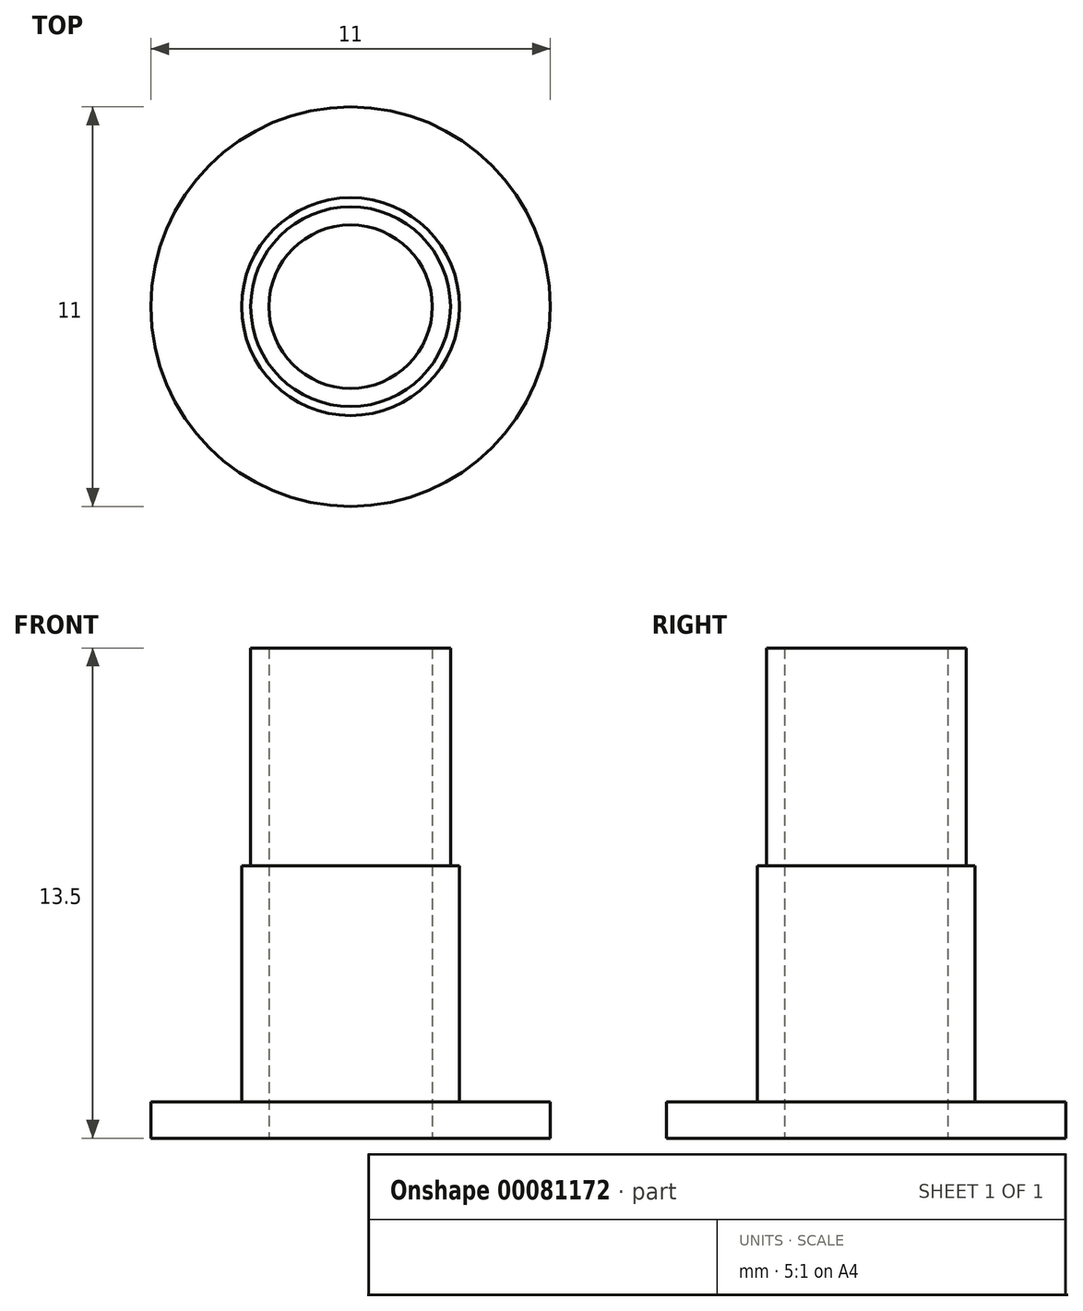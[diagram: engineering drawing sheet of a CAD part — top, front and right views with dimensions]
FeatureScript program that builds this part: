
annotation { "Feature Type Name" : "Feature", "Feature Type Description" : "" }
export const myFeature = defineFeature(function(context is Context, id is Id, definition is map)
    precondition{}
    {
        {
            var Q0;
            Q0=qCreatedBy(makeId("Top.planeOp"),FACE);
            var sketch = newSketch(context, id + "F0", { "sketchPlane" : qUnion([Q0])});
            skCircle(sketch, "E0", {"center": v(0, 0) * mm, "radius": 2.25 * mm});
            skCircle(sketch, "E1", {"center": v(0, 0) * mm, "radius": 5.5 * mm});
            skSolve(sketch);
        }
        {
            var Q0;
            Q0=qSketchRegion(id+"F0",true);
            extrude(context, id + "F1", {"entities" : qUnion([Q0]), "depth" : 13.5 * mm});
        }
        {
            var Q0;
            Q0=makeQuery(id+"F1.opExtrude","CAP_FACE",FACE,{"disambiguationData":[OSD([sQuery(id+"F0.wireOp",EDGE,"E0"),sQuery(id+"F0.wireOp",EDGE,"E1")])],"isStart":false});
            var sketch = newSketch(context, id + "F2", { "sketchPlane" : qUnion([Q0])});
            skCircle(sketch, "E2", {"center": v(0, 0) * mm, "radius": 3 * mm});
            skSolve(sketch);
        }
        {
            var Q0;
            Q0=makeQuery(id+"F2.imprint","IMPRINT",FACE,{"disambiguationData":[TD([[makeQuery(id+"F2.imprint","IMPRINT",EDGE,{"derivedFrom":sQuery(id+"F2.wireOp",EDGE,"E2")}),-1.0]])]});
            extrude(context, id + "F3", {"entities" : qUnion([Q0]), "operationType" : NewBodyOperationType.REMOVE, "oppositeDirection" : true, "depth" : 12.5 * mm});
        }
        {
            var Q0;
            Q0=makeQuery(id+"F1.opExtrude","CAP_FACE",FACE,{"disambiguationData":[OSD([sQuery(id+"F0.wireOp",EDGE,"E0"),sQuery(id+"F0.wireOp",EDGE,"E1")])],"isStart":false});
            var sketch = newSketch(context, id + "F4", { "sketchPlane" : qUnion([Q0])});
            skCircle(sketch, "E3", {"center": v(0, 0) * mm, "radius": 2.75 * mm});
            skSolve(sketch);
        }
        {
            var Q0;
            Q0=makeQuery(id+"F4.imprint","IMPRINT",FACE,{"disambiguationData":[TD([[makeQuery(id+"F4.imprint","IMPRINT",EDGE,{"derivedFrom":sQuery(id+"F4.wireOp",EDGE,"E3")}),-1.0]])]});
            extrude(context, id + "F5", {"entities" : qUnion([Q0]), "operationType" : NewBodyOperationType.REMOVE, "oppositeDirection" : true, "depth" : 6 * mm});
        }
    });
